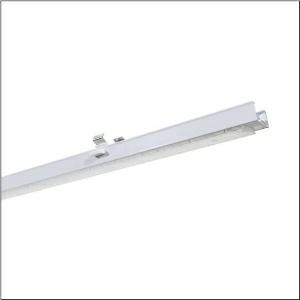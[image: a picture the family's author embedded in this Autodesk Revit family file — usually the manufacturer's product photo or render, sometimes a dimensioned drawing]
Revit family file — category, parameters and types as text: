
# Revit family: trunking_flex_31_51re12mb5cb
name_source: partatom
category: Lighting Fixtures
units: mm (PartAtom-declared; Revit-internal decimal feet)

## family parameters
Cut with Voids When Loaded = No
Host = Face
Light Source = No
Part Type = Normal
Room Calculation Point = No
Round Connector Dimension = Use Diameter
Shared = No

## types (1)
- --- (1 x LED, 11500 lm, 66 W, 5000K)
    Apparent Load = 66 VA
    CIE Flux Codes = 65 91 98 99 100
    Color Rendering = 80
    Color Temperature = 5000K
    Default Elevation = 1800 mm
    Description = Trunking Flex 31, luminaire insert, of extruded aluminium section, coated, traffic white (RAL 9016), length: 1.472mm, width: 91mm, height: 53mm, LED rated luminous flux: 11.500lm, light colour: 850, control gear: ON/OFF Multilumen, with system connector: socket, mains connection: 220..240V, AC, 50/60Hz, rated input power: 66W, luminous flux adjustable on luminaire in eight steps (3450/4380/5800/6700/8350/9200/10500/11500lm ), connected load according to luminous flux setting (19/24/32/37/47/52/60/66W), primary light control with lens, of plastic, primary optical cover: cover, of PMMA, light emission: direct distribution, protection rating (complete): IP20, insulation class (complete): insulation class I (protective earthing), certification: CE, UKCA, impact resistance: IK02, permissible ambient temperature for indoor applications: -20..+40°C, packaging unit: 1 piece
    Height = 58 mm
    Lamp = 1 x LED
    Lamp Light Flux = 11500 lm
    Lamp Power = 66 W
    Lamp count = 1
    Length = 1472 mm
    Luminous efficacy = 174 lm/W
    Manufacturer = Siteco
    ModVariant = No
    Model = 51RE12MB5CB
    Mounting Place = Ceiling
    Mounting Type = Pendant
    Number of Poles = 1
    OnlyDefault = Yes
    Power Factor = 1
    Product Name = Trunking Flex 31
    Product group = luminaire insert
    ProductGroupID = 902
    Protection Class = Protection class I
    Protection Degree = IP 20
    RLX_Detail_Level = 1
    RLX_Emergency_Light_Flux = 0 lm
    RLX_Emergency_Type = 0
    RLX_Emergency_Type_DB = No
    RlxData = <blob elided: 21053 chars, md5=c6560031>
    Socket = socket
    Standby Power = 0 W
    System Light Flux = 11500 lm
    System Power = 66 W
    Type Comments = factory setting: luminous flux: 100 % | (ON | ON | ON)
    Type Image = l_1266702.jpg
    URL = http://relux.com
    VarID = @adj_059126
    Voltage = 0 V
    Weight = 0.00 kg
    Width = 65 mm

## geometry (parser evidence)
native form markers: Blend x4, Sweep x9
no freeform markers — native parametric forms only
